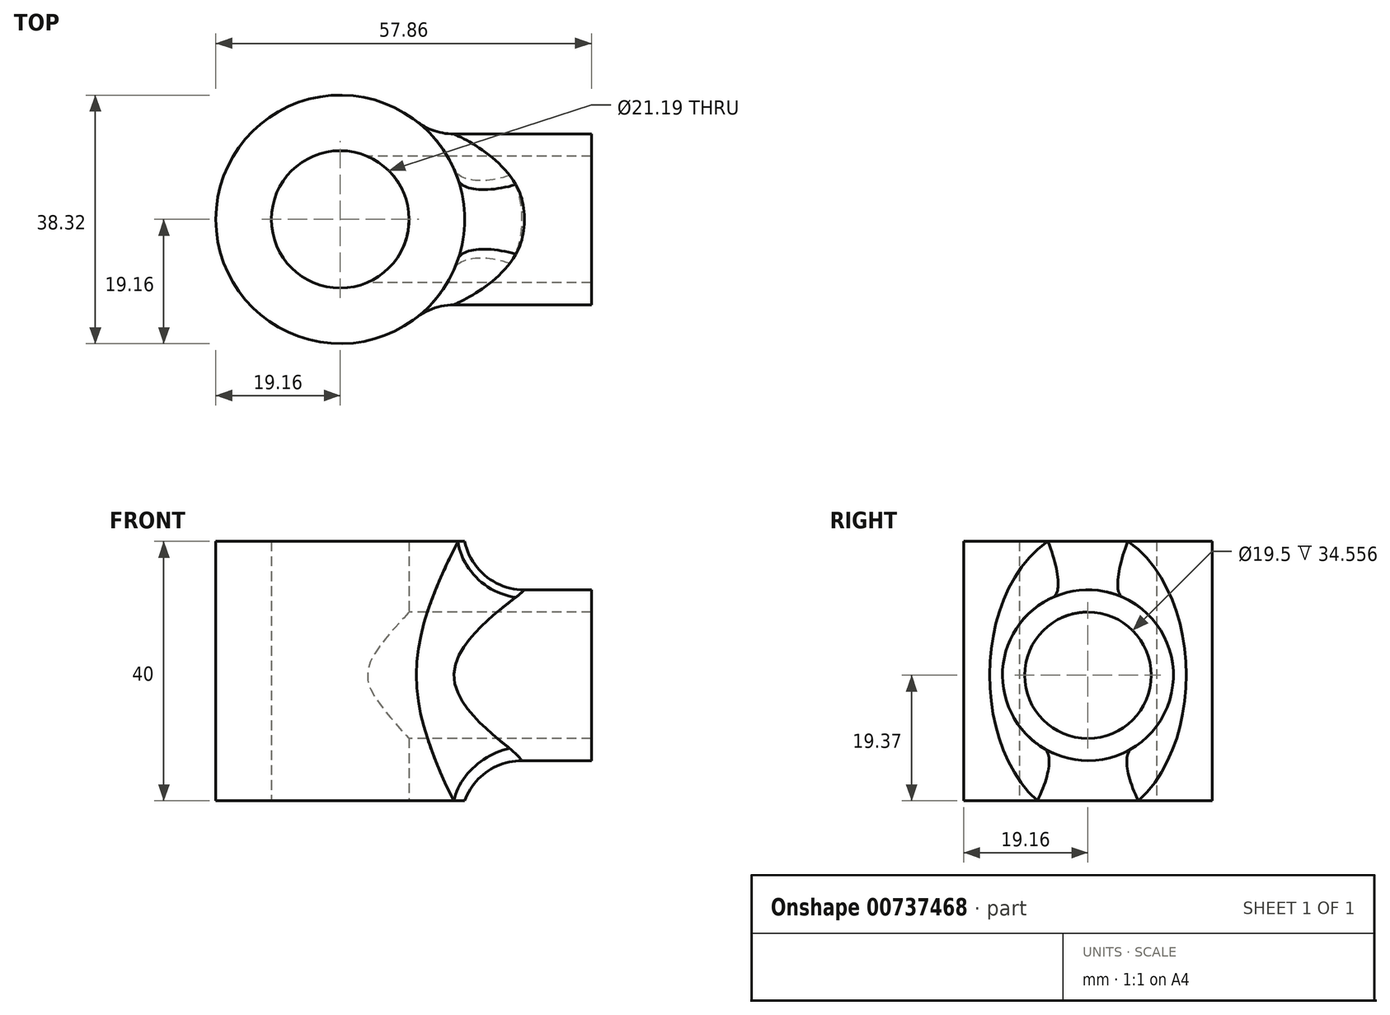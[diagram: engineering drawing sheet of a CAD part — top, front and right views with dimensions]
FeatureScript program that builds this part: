
annotation { "Feature Type Name" : "Feature", "Feature Type Description" : "" }
export const myFeature = defineFeature(function(context is Context, id is Id, definition is map)
    precondition{}
    {
        {
            var Q0;
            Q0=qCreatedBy(makeId("Top.planeOp"),FACE);
            var sketch = newSketch(context, id + "F0", { "sketchPlane" : qUnion([Q0])});
            skCircle(sketch, "E0", {"center": v(0, 0) * mm, "radius": 19.16 * mm});
            skCircle(sketch, "E1", {"center": v(0, 0) * mm, "radius": 10.6 * mm});
            skSolve(sketch);
        }
        {
            var Q0;
            Q0 = qSketchRegion(id + "F0", true);
            extrude(context, id + "F1", {"entities" : qUnion([Q0]), "depth" : 40 * mm, "offsetDistance" : 25 * mm});
        }
        {
            var Q0;
            Q0=qCreatedBy(makeId("Right.planeOp"),FACE);
            cPlane(context, id + "F2", {"entities" : qUnion([Q0]), "cplaneType" : CPlaneType.OFFSET, "offset" : 13.7 * mm, "width" : 150 * mm, "height" : 150 * mm});
        }
        {
            var Q0;
            Q0=qCreatedBy(id+"F2.planeOp",FACE);
            var sketch = newSketch(context, id + "F3", { "sketchPlane" : qUnion([Q0])});
            skCircle(sketch, "E2", {"center": v(0, 19.37) * mm, "radius": 9.75 * mm});
            skCircle(sketch, "E3", {"center": v(0, 19.37) * mm, "radius": 13.17 * mm});
            skSolve(sketch);
        }
        {
            var Q0;
            Q0=makeQuery(id+"F3.imprint","IMPRINT",FACE,{"disambiguationData":[TD([[makeQuery(id+"F3.imprint","IMPRINT",EDGE,{"derivedFrom":sQuery(id+"F3.wireOp",EDGE,"E2")}),1.0]])]});
            extrude(context, id + "F4", {"entities" : qUnion([Q0]), "operationType" : NewBodyOperationType.REMOVE, "endBound" : BoundingType.SYMMETRIC, "depth" : 34.4 * mm, "offsetDistance" : 25 * mm});
        }
        {
            var Q0;
            Q0 = qSketchRegion(id + "F3", true);
            extrude(context, id + "F5", {"entities" : qUnion([Q0]), "operationType" : NewBodyOperationType.ADD, "depth" : 25 * mm, "offsetDistance" : 25 * mm});
        }
        {
            var Q0;
            Q0=makeQuery(id+"F5.boolean.opBoolean","INTERSECT",EDGE,{"derivedFrom":[makeQuery(id+"F1.opExtrude","SWEPT_FACE",FACE,{"disambiguationData":[OSD([sQuery(id+"F0.wireOp",EDGE,"E0")])]}),makeQuery(id+"F5.opExtrude","SWEPT_FACE",FACE,{"disambiguationData":[OSD([sQuery(id+"F3.wireOp",EDGE,"E3")])]})]});
            fillet(context, id + "F6", {"entities" : qUnion([Q0]), "radius" : 9.42 * mm, "tangentPropagation" : true, "allowEdgeOverflow" : false});
        }
    });
